# Revit family: 49480XXX_01.3dm
name_source: partatom
category: Plumbing Fixtures
units: mm (PartAtom-declared; Revit-internal decimal feet)

## family parameters
Always vertical = Yes
Cut with Voids When Loaded = No
OmniClass Number = 23.31.11.00
OmniClass Title = Faucets
Part Type = Normal
Room Calculation Point = No
Round Connector Dimension = Use Diameter
Shared = No
Work Plane-Based = No

## types (1)
- Default - please load Revit Family Type Catalog
    Default Elevation = 1219 mm
    Description = AXOR Citterio C 3-hole bath mixer for concealed installation wall-mounted with hand shower
    Manufacturer = AXOR
    Material = AXOR - Metal - 000 Chrome
    Model = 49480XXX
    Product Guid = cde01466-21e1-4de3-9623-fd3371b5afda
    Product Page URL = https://www.axor-design.com
    Product data url = https://bimobject.com
    URL = https://www.axor-design.com
    Version = 0

## geometry (parser evidence)
native form markers: Sweep x2
no freeform markers — native parametric forms only
